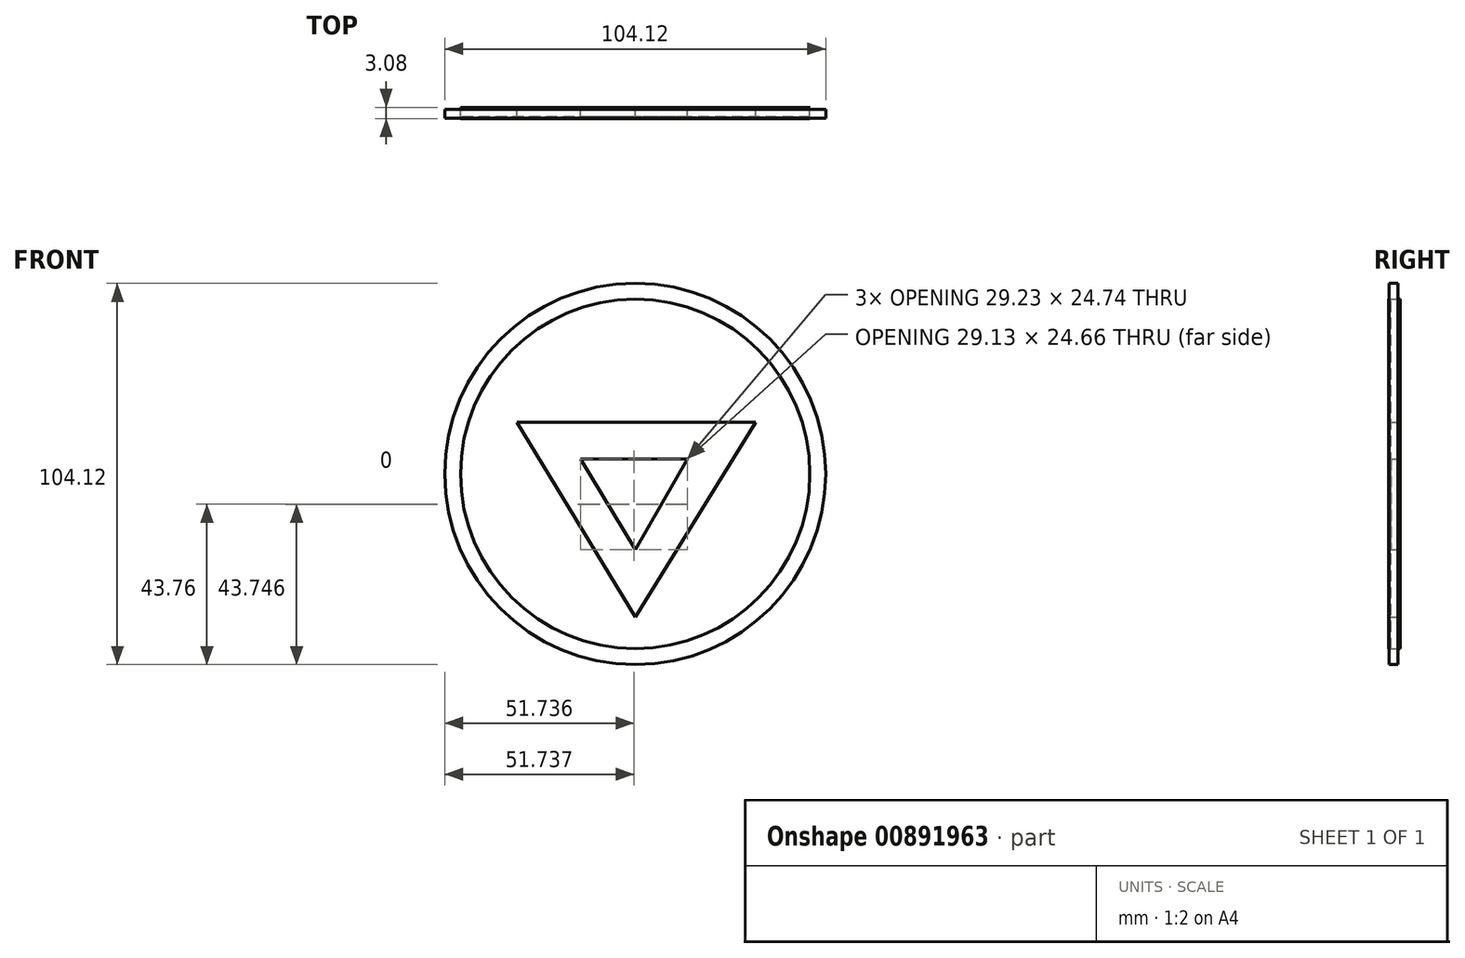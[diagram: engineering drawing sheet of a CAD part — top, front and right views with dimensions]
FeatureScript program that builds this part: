
annotation { "Feature Type Name" : "Feature", "Feature Type Description" : "" }
export const myFeature = defineFeature(function(context is Context, id is Id, definition is map)
    precondition{}
    {
        {
            var Q0;
            Q0=qCreatedBy(makeId("Front.planeOp"),FACE);
            var sketch = newSketch(context, id + "F0", { "sketchPlane" : qUnion([Q0])});
            skCircle(sketch, "E0", {"center": v(0, 0) * mm, "radius": 47.73 * mm});
            skLineSegment(sketch, "E1", {"start": v(0, -47.73) * mm, "end": v(43.62, 19.37) * mm});
            skLineSegment(sketch, "E2", {"start": v(43.62, 19.37) * mm, "end": v(-43.62, 19.37) * mm});
            skLineSegment(sketch, "E3", {"start": v(-43.62, 19.37) * mm, "end": v(0, -47.73) * mm});
            skLineSegment(sketch, "E4", {"start": v(0, -11.35) * mm, "end": v(7.38, 0) * mm});
            skLineSegment(sketch, "E5", {"start": v(7.38, 0) * mm, "end": v(-7.33, 0) * mm});
            skLineSegment(sketch, "E6", {"start": v(-7.33, 0) * mm, "end": v(0, -11.35) * mm});
            skLineSegment(sketch, "E7", {"start": v(0, -20.68) * mm, "end": v(14.3, 4.06) * mm});
            skLineSegment(sketch, "E8", {"start": v(14.3, 4.06) * mm, "end": v(-14.94, 4.06) * mm});
            skLineSegment(sketch, "E9", {"start": v(-14.94, 4.06) * mm, "end": v(0, -20.68) * mm});
            skLineSegment(sketch, "E10", {"start": v(14.3, 4.06) * mm, "end": v(43.62, 19.37) * mm});
            skLineSegment(sketch, "E11", {"start": v(-14.94, 4.06) * mm, "end": v(-43.62, 19.37) * mm});
            skLineSegment(sketch, "E12", {"start": v(0, -47.73) * mm, "end": v(0, -20.68) * mm});
            skSolve(sketch);
        }
        {
            var Q0;
            Q0=qCreatedBy(makeId("Front.planeOp"),FACE);
            var sketch = newSketch(context, id + "F1", { "sketchPlane" : qUnion([Q0])});
            skCircle(sketch, "E13", {"center": v(0, 0) * mm, "radius": 52.06 * mm});
            skSolve(sketch);
        }
        {
            var Q0;
            Q0=qCreatedBy(makeId("Front.planeOp"),FACE);
            var sketch = newSketch(context, id + "F2", { "sketchPlane" : qUnion([Q0])});
            skLineSegment(sketch, "E14", {"start": v(0, -39.08) * mm, "end": v(32.96, 14.07) * mm});
            skLineSegment(sketch, "E15", {"start": v(32.96, 14.07) * mm, "end": v(-32.35, 14.07) * mm});
            skLineSegment(sketch, "E16", {"start": v(-32.35, 14.07) * mm, "end": v(0, -39.08) * mm});
            skSolve(sketch);
        }
        {
            var Q0;
            Q0=makeQuery(id+"F0.imprint","IMPRINT",FACE,{"disambiguationData":[TD([[makeQuery(id+"F0.imprint","IMPRINT",EDGE,{"derivedFrom":sQuery(id+"F0.wireOp",EDGE,"E2")}),1.0]])]});
            var Q1;
            Q1=makeQuery(id+"F2.imprint","IMPRINT",FACE,{"disambiguationData":[TD([[makeQuery(id+"F2.imprint","IMPRINT",EDGE,{"derivedFrom":sQuery(id+"F2.wireOp",EDGE,"E14")}),1.0]])]});
            var Q2;
            Q2 = qSketchRegion(id + "F2", true);
            var Q3;
            Q3 = qSketchRegion(id + "F0", true);
            var Q4;
            Q4=makeQuery(id+"F0.imprint","IMPRINT",FACE,{"disambiguationData":[TD([[makeQuery(id+"F0.imprint","IMPRINT",EDGE,{"derivedFrom":sQuery(id+"F0.wireOp",EDGE,"E3")}),1.0]])]});
            var Q5;
            Q5=makeQuery(id+"F0.imprint","IMPRINT",FACE,{"disambiguationData":[TD([[makeQuery(id+"F0.imprint","IMPRINT",EDGE,{"derivedFrom":sQuery(id+"F0.wireOp",EDGE,"E1")}),1.0]])]});
            extrude(context, id + "F3", {"entities" : qUnion([Q0, Q1, Q2, Q3, Q4, Q5]), "depth" : 2.54 * mm, "offsetDistance" : 25.4 * mm});
        }
        {
            var Q0;
            Q0=makeQuery(id+"F1.imprint","IMPRINT",FACE,{"disambiguationData":[TD([[makeQuery(id+"F1.imprint","IMPRINT",EDGE,{"derivedFrom":sQuery(id+"F1.wireOp",EDGE,"E13")}),1.0]])]});
            var Q1;
            Q1 = qSketchRegion(id + "F1", true);
            var Q2;
            Q2 = qSketchRegion(id + "F0", true);
            extrude(context, id + "F4", {"entities" : qUnion([Q0, Q1, Q2]), "depth" : 2.4 * mm, "offsetDistance" : 25.4 * mm});
        }
        {
            var Q0;
            Q0 = qSketchRegion(id + "F0", true);
            var Q1;
            Q1=makeQuery(id+"F3.opExtrude","CAP_FACE",FACE,{"disambiguationData":[OSD([sQuery(id+"F0.wireOp",EDGE,"E0"),sQuery(id+"F0.wireOp",EDGE,"E7"),sQuery(id+"F0.wireOp",EDGE,"E8"),sQuery(id+"F0.wireOp",EDGE,"E9")])],"isStart":false});
            extrude(context, id + "F5", {"entities" : qUnion([Q0, Q1]), "oppositeDirection" : true, "depth" : 0.54 * mm, "offsetDistance" : 25.4 * mm, "hasDraft" : true, "draftAngle" : 3 * degree});
        }
    });
